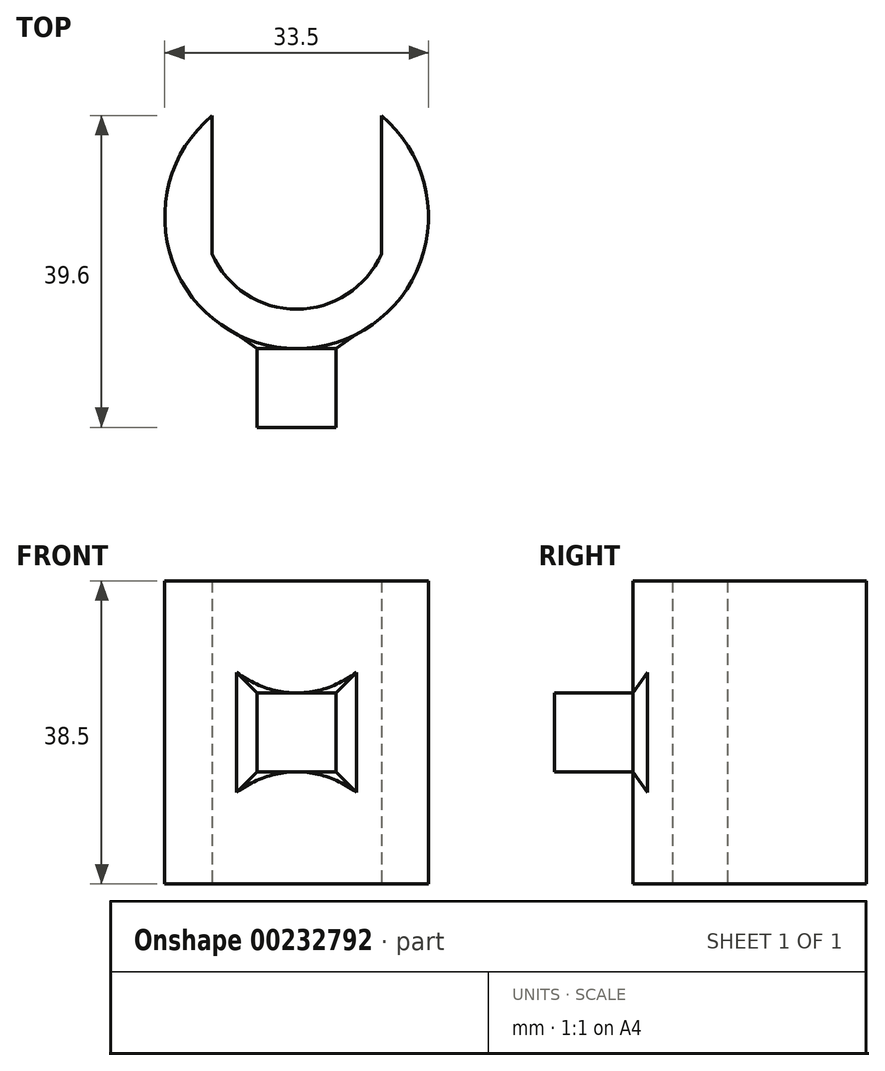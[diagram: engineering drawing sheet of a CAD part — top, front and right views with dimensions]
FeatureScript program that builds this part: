
annotation { "Feature Type Name" : "Feature", "Feature Type Description" : "" }
export const myFeature = defineFeature(function(context is Context, id is Id, definition is map)
    precondition{}
    {
        {
            var Q0;
            Q0=qCreatedBy(makeId("Top.planeOp"),FACE);
            var sketch = newSketch(context, id + "F0", { "sketchPlane" : qUnion([Q0])});
            skArc(sketch, "E0", {"start": v(-10.75, -4.74) * mm, "mid": v(0, -11.75) * mm, "end": v(10.75, -4.74) * mm});
            skArc(sketch, "E1", {"start": v(-10.75, 12.85) * mm, "mid": v(0, -16.75) * mm, "end": v(10.75, 12.85) * mm});
            skLineSegment(sketch, "E2.left", {"start": v(-10.75, 12.85) * mm, "end": v(-10.75, -4.74) * mm});
            skLineSegment(sketch, "E2.right", {"start": v(10.75, 12.85) * mm, "end": v(10.75, -4.74) * mm});
            skSolve(sketch);
        }
        {
            var Q0;
            Q0 = qSketchRegion(id + "F0", true);
            extrude(context, id + "F1", {"entities" : qUnion([Q0]), "depth" : 38.5 * mm});
        }
        {
            var Q0;
            Q0=qCreatedBy(makeId("Front.planeOp"),FACE);
            cPlane(context, id + "F2", {"entities" : qUnion([Q0]), "cplaneType" : CPlaneType.OFFSET, "offset" : 16.75 * mm, "width" : 150 * mm, "height" : 150 * mm});
        }
        {
            var Q0;
            Q0=qCreatedBy(id+"F2.planeOp",FACE);
            var sketch = newSketch(context, id + "F3", { "sketchPlane" : qUnion([Q0])});
            skLineSegment(sketch, "E3.bottom", {"start": v(-5, 24.25) * mm, "end": v(5, 24.25) * mm});
            skLineSegment(sketch, "E3.top", {"start": v(-5, 14.25) * mm, "end": v(5, 14.25) * mm});
            skLineSegment(sketch, "E3.left", {"start": v(-5, 24.25) * mm, "end": v(-5, 14.25) * mm});
            skLineSegment(sketch, "E3.right", {"start": v(5, 24.25) * mm, "end": v(5, 14.25) * mm});
            skPoint(sketch, "E3.middle", {"position": v(0, 19.25) * mm});
            skSolve(sketch);
        }
        {
            var Q0;
            Q0 = qSketchRegion(id + "F3", true);
            extrude(context, id + "F4", {"entities" : qUnion([Q0]), "operationType" : NewBodyOperationType.ADD, "depth" : 10 * mm, "hasSecondDirection" : true, "secondDirectionOppositeDirection" : true, "secondDirectionDepth" : 4 * mm, "hasSecondDirectionDraft" : true, "secondDirectionDraftAngle" : 55 * degree});
        }
    });
